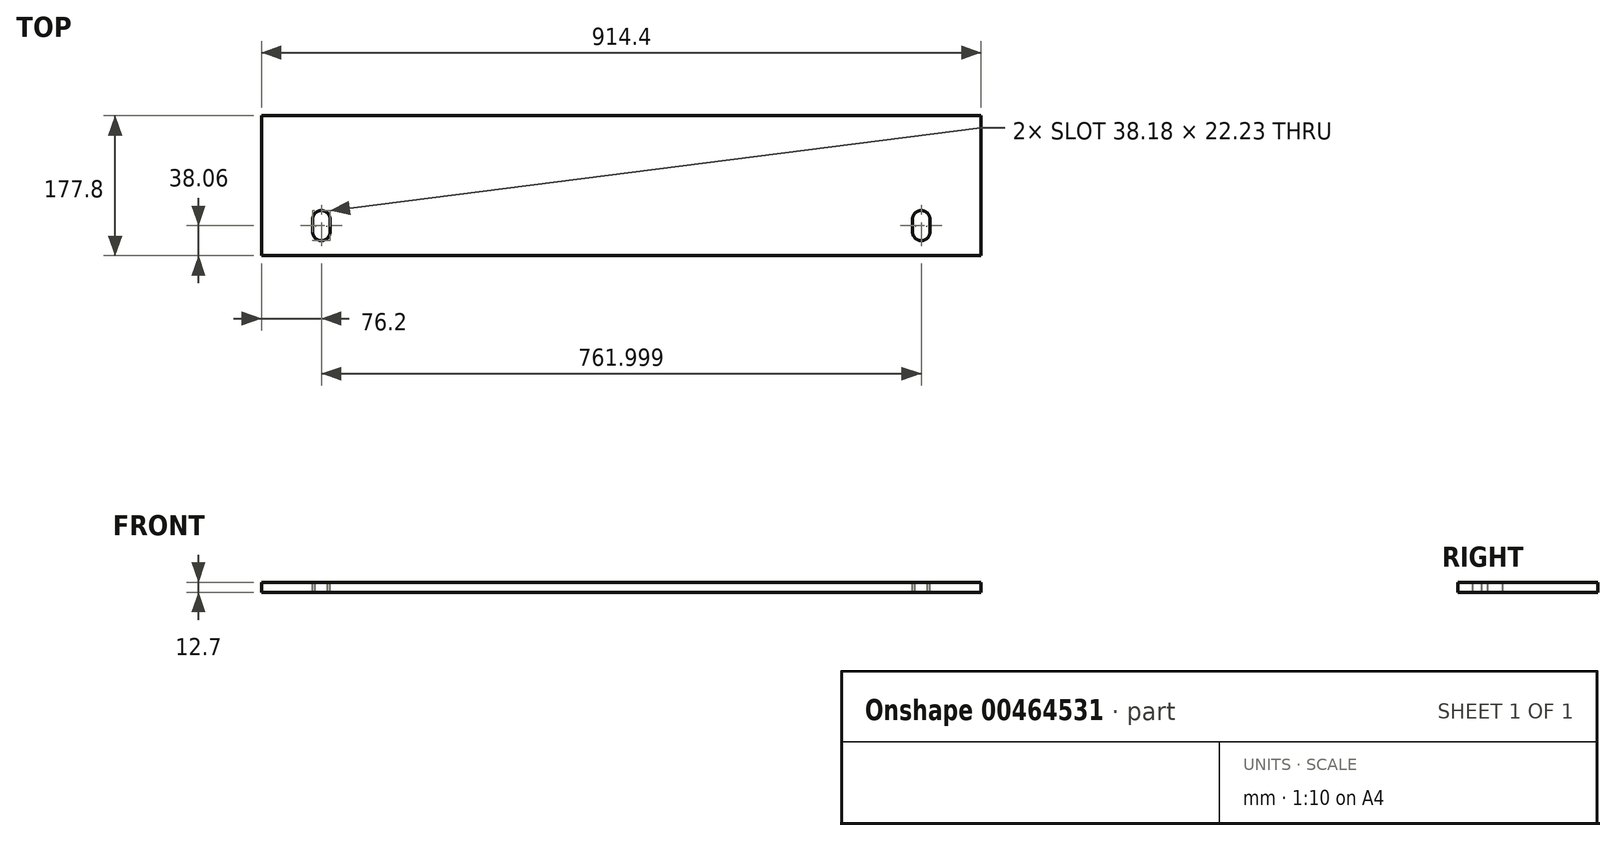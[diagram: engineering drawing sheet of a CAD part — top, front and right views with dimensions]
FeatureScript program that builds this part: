
annotation { "Feature Type Name" : "Feature", "Feature Type Description" : "" }
export const myFeature = defineFeature(function(context is Context, id is Id, definition is map)
    precondition{}
    {
        {
            var Q0;
            Q0=qCreatedBy(makeId("Top.planeOp"),FACE);
            var sketch = newSketch(context, id + "F0", { "sketchPlane" : qUnion([Q0])});
            skLineSegment(sketch, "E0.bottom", {"start": v(457.2, -88.9) * mm, "end": v(-457.2, -88.9) * mm});
            skLineSegment(sketch, "E0.top", {"start": v(457.2, 88.9) * mm, "end": v(-457.2, 88.9) * mm});
            skLineSegment(sketch, "E0.left", {"start": v(457.2, -88.9) * mm, "end": v(457.2, 88.9) * mm});
            skLineSegment(sketch, "E0.right", {"start": v(-457.2, -88.9) * mm, "end": v(-457.2, 88.9) * mm});
            skPoint(sketch, "E0.middle", {"position": v(0, 0) * mm});
            skSolve(sketch);
        }
        {
            var Q0;
            Q0 = qSketchRegion(id + "F0", true);
            extrude(context, id + "F1", {"entities" : qUnion([Q0]), "depth" : 12.7 * mm});
        }
        {
            var Q0;
            Q0=makeQuery(id+"F1.opExtrude","CAP_FACE",FACE,{"disambiguationData":[OSD([sQuery(id+"F0.wireOp",EDGE,"E0.bottom"),sQuery(id+"F0.wireOp",EDGE,"E0.top"),sQuery(id+"F0.wireOp",EDGE,"E0.left"),sQuery(id+"F0.wireOp",EDGE,"E0.right")])],"isStart":false});
            var sketch = newSketch(context, id + "F2", { "sketchPlane" : qUnion([Q0])});
            skPoint(sketch, "E1.middle", {"position": v(-381, -50.8) * mm});
            skLineSegment(sketch, "E2", {"start": v(-388.78, -50.8) * mm, "end": v(-388.7, -50.8) * mm});
            skPoint(sketch, "E3.third.point", {"position": v(-381, -31.75) * mm});
            skArc(sketch, "E4", {"start": v(-392.11, -58.67) * mm, "mid": v(-381.08, -69.93) * mm, "end": v(-369.89, -58.82) * mm});
            skArc(sketch, "E5", {"start": v(-373.26, -50.84) * mm, "mid": v(-373.24, -50.82) * mm, "end": v(-373.22, -50.8) * mm});
            skLineSegment(sketch, "E6", {"start": v(-392.11, -42.89) * mm, "end": v(-392.11, -58.97) * mm, "construction": true});
            skLineSegment(sketch, "E7", {"start": v(-369.89, -42.89) * mm, "end": v(-369.89, -58.97) * mm, "construction": true});
            skLineSegment(sketch, "E8", {"start": v(-392.11, -42.89) * mm, "end": v(-392.11, -58.97) * mm});
            skLineSegment(sketch, "E9", {"start": v(-369.89, -42.89) * mm, "end": v(-369.89, -58.97) * mm});
            skArc(sketch, "E10.trimOffspring", {"start": v(-388.78, -50.8) * mm, "mid": v(-388.76, -50.82) * mm, "end": v(-388.74, -50.84) * mm});
            skArc(sketch, "E11.trimOffspring", {"start": v(-388.7, -50.8) * mm, "mid": v(-388.72, -50.82) * mm, "end": v(-388.74, -50.84) * mm});
            skLineSegment(sketch, "E12.trimOffspring", {"start": v(-373.3, -50.8) * mm, "end": v(-373.22, -50.8) * mm});
            skArc(sketch, "E13.trimOffspring", {"start": v(-369.89, -42.89) * mm, "mid": v(-381, -31.75) * mm, "end": v(-392.11, -42.89) * mm});
            skArc(sketch, "E14.trimOffspring", {"start": v(-373.26, -50.84) * mm, "mid": v(-373.28, -50.82) * mm, "end": v(-373.3, -50.8) * mm});
            skLineSegment(sketch, "E15.MirrorCS", {"start": v(373.3, -50.8) * mm, "end": v(373.22, -50.8) * mm});
            skArc(sketch, "E16.MirrorCS", {"start": v(388.78, -50.8) * mm, "mid": v(388.76, -50.82) * mm, "end": v(388.74, -50.84) * mm});
            skArc(sketch, "E17.MirrorCS", {"start": v(388.7, -50.8) * mm, "mid": v(388.72, -50.82) * mm, "end": v(388.74, -50.84) * mm});
            skArc(sketch, "E18.MirrorCS", {"start": v(373.26, -50.84) * mm, "mid": v(373.28, -50.82) * mm, "end": v(373.3, -50.8) * mm});
            skArc(sketch, "E19.MirrorCS", {"start": v(373.26, -50.84) * mm, "mid": v(373.24, -50.82) * mm, "end": v(373.22, -50.8) * mm});
            skLineSegment(sketch, "E20.MirrorCS", {"start": v(388.78, -50.8) * mm, "end": v(388.7, -50.8) * mm});
            skLineSegment(sketch, "E21.MirrorCS", {"start": v(392.11, -42.89) * mm, "end": v(392.11, -58.97) * mm});
            skLineSegment(sketch, "E22.MirrorCS", {"start": v(369.89, -42.89) * mm, "end": v(369.89, -58.97) * mm});
            skArc(sketch, "E23.MirrorCS", {"start": v(369.89, -42.89) * mm, "mid": v(381, -31.75) * mm, "end": v(392.11, -42.89) * mm});
            skLineSegment(sketch, "E24.MirrorCS", {"start": v(392.11, -42.89) * mm, "end": v(392.11, -58.97) * mm, "construction": true});
            skPoint(sketch, "E25.MirrorP", {"position": v(381, -50.8) * mm});
            skLineSegment(sketch, "E26.MirrorCS", {"start": v(369.89, -42.89) * mm, "end": v(369.89, -58.97) * mm, "construction": true});
            skArc(sketch, "E27.MirrorCS", {"start": v(392.11, -58.67) * mm, "mid": v(381.08, -69.93) * mm, "end": v(369.89, -58.82) * mm});
            skPoint(sketch, "E28.MirrorP", {"position": v(381, -31.75) * mm});
            skSolve(sketch);
        }
        {
            var Q0;
            Q0 = qSketchRegion(id + "F2", true);
            extrude(context, id + "F3", {"entities" : qUnion([Q0]), "operationType" : NewBodyOperationType.REMOVE, "oppositeDirection" : true, "depth" : 25.4 * mm});
        }
    });
